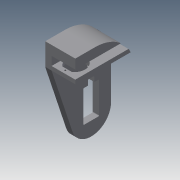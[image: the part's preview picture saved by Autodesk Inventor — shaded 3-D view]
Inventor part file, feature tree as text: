
AUTODESK INVENTOR PART (.ipt)
format: ipt  version: 2013 (Build 170138000, 138)  size: 444,928 bytes
history: native  units: mm
features: sketch x35, extrude x31, fillet x1
ambient origin geometry x8: Origin, YZ Plane, XZ Plane, XY Plane, X Axis, Y Axis, Z Axis, Center Point
bodies: Solid1 (feature_tree)
feature tree (67):
  extrude  "Extrusion1"  Depth=66.3mm
  extrude  "Extrusion2"  Depth=55.0mm
  extrude  "Extrusion3"  Depth=55.0mm
  extrude  "Extrusion4"  Depth=9.9mm
  extrude  "Extrusion5"  Depth=9.9mm
  extrude  "Extrusion6"  Depth=3.0mm
  extrude  "Extrusion7"  Depth=3.0mm
  extrude  "Extrusion8"  Depth=13.6mm
  extrude  "Extrusion9"  Depth=45.0mm
  sketch  "Sketch10"  dims[d22=15.0mm d23=5.0mm d24=0.0mm]
  extrude  "Extrusion10"  Depth=5.0mm TaperAngle=0.0deg
  extrude  "Extrusion11"  Depth=55.0mm
  extrude  "Extrusion12"  Depth=20.0mm
  sketch  "Sketch14"  dims[d33=10.0mm d34=32.9mm d35=0.0mm]
  extrude  "Extrusion13"  Depth=5.0mm TaperAngle=0.0deg
  extrude  "Extrusion14"  Depth=32.9mm TaperAngle=0.0deg
  extrude  "Extrusion15"  Depth=25.0mm
  extrude  "Extrusion16"  Depth=5.0mm TaperAngle=0.0deg
  extrude  "Extrusion17"  Depth=15.0mm
  sketch  "Sketch20"  dims[d50=28.0mm d51=5.0mm d52=0.0mm]
  extrude  "Extrusion18"  Depth=18.0mm
  extrude  "Extrusion19"  Depth=32.9mm TaperAngle=0.0deg
  extrude  "Extrusion20"  Depth=5.0mm TaperAngle=0.0deg
  extrude  "Extrusion21"  Depth=5.0mm
  extrude  "Extrusion22"  Depth=13.6mm
  extrude  "Extrusion23"  Depth=12.5mm
  sketch  "Sketch27"  dims[d68=21.4mm d69=2.0mm]
  extrude  "Extrusion24"  Depth=12.2mm
  extrude  "Extrusion25"  Depth=5.0mm TaperAngle=0.0deg
  extrude  "Extrusion26"  Depth=2.0mm
  extrude  "Extrusion27"  Depth=2.0mm
  sketch  "Sketch32"  dims[d81=2.0mm]
  sketch  "Sketch33"  dims[d82=5.0mm d83=0.0mm]
  extrude  "Extrusion28"  Depth=2.05mm
  extrude  "Extrusion29"  Depth=5.0mm TaperAngle=0.0deg
  extrude  "Extrusion30"  Depth=2.05mm
  extrude  "Extrusion31"  Depth=10.6mm
  fillet  "Fillet1"  Radius=2.05mm
  sketch  "Sketch1"  dims[d0=33.15mm d2=66.3mm]
  sketch  "Sketch2"  dims[d4=18.1mm d5=55.0mm]
  sketch  "Sketch3"  dims[d6=20.0mm d7=55.0mm]
  sketch  "Sketch4"  dims[d8=40.2mm d9=9.9mm]
  sketch  "Sketch5"  dims[d10=9.5mm d11=9.9mm]
  sketch  "Sketch6"  dims[d12=9.5mm d13=3.0mm]
  sketch  "Sketch7"  dims[d14=3.0mm d15=3.0mm]
  sketch  "Sketch8"  dims[d16=3.0mm d17=13.6mm]
  sketch  "Sketch9"  dims[d20=25.0mm d21=45.0mm]
  sketch  "Sketch11"  dims[d25=18.1mm d26=55.0mm]
  sketch  "Sketch12"  dims[d27=40.2mm d28=20.0mm]
  sketch  "Sketch13"  dims[d29=5.0mm d30=0.0mm d31=5.0mm d32=0.0mm]
  sketch  "Sketch15"  dims[d36=25.0mm d37=0.0mm d38=25.0mm]
  sketch  "Sketch16"  dims[d39=10.0mm d40=5.0mm d41=0.0mm]
  sketch  "Sketch17"  dims[d42=12.5mm d43=15.0mm]
  sketch  "Sketch18"  dims[d44=10.0mm d45=0.0mm d46=18.0mm]
  sketch  "Sketch19"  dims[d47=5.0mm d48=32.9mm d49=0.0mm]
  sketch  "Sketch21"  dims[d53=10.0mm d54=0.0mm d55=5.0mm]
  sketch  "Sketch22"  dims[d56=12.5mm d57=13.6mm]
  sketch  "Sketch23"  dims[d58=10.0mm d59=0.0mm d60=12.5mm]
  sketch  "Sketch24"  dims[d61=12.4mm d62=12.2mm]
  sketch  "Sketch25"  dims[d63=6.2mm d64=5.0mm d65=0.0mm]
  sketch  "Sketch26"  dims[d66=10.6mm d67=2.0mm]
  sketch  "Sketch28"  dims[d70=5.0mm d71=0.0mm d72=2.05mm]
  sketch  "Sketch29"  dims[d73=2.05mm d74=5.0mm d75=0.0mm]
  sketch  "Sketch30"  dims[d76=21.4mm d77=2.05mm]
  sketch  "Sketch31"  dims[d78=2.0mm d79=10.6mm d80=2.05mm]
  sketch  "Sketch34"  dims[d84=45.0mm]
  sketch  "Sketch35"  dims[d86=5.0mm d87=5.0mm d88=39.0mm d89=0.0mm d90=22.0mm d91=5.0mm d92=0.0mm d93=3.0mm d94=0.0mm d95=10.0mm d96=2.0mm d97=0.0mm d98=2.0mm d99=0.0mm d100=10.25mm d101=7.25mm d102=22.0mm d103=0.0mm d104=10.0mm d105=2.0mm d106=0.0mm d107=10.0mm d108=3.0mm d109=0.0mm d111=14.0mm d112=14.0mm d113=5.0mm d114=0.0mm d115=29.9mm d116=0.0mm d117=70.0mm d118=0.0mm d119=68.0mm d120=2.0mm d121=5.0mm d122=37.9mm d123=0.0mm d124=28.0mm d125=70.0mm d126=25.0mm d127=25.0mm d128=50.0mm d129=37.9mm d130=0.0mm d131=8.0mm d132=0.0mm d133=12.0mm d134=90.0deg d135=29.9mm d136=0.0mm d137=47.0mm d138=8.0mm d139=8.0mm d140=0.0mm d141=1.0mm]
